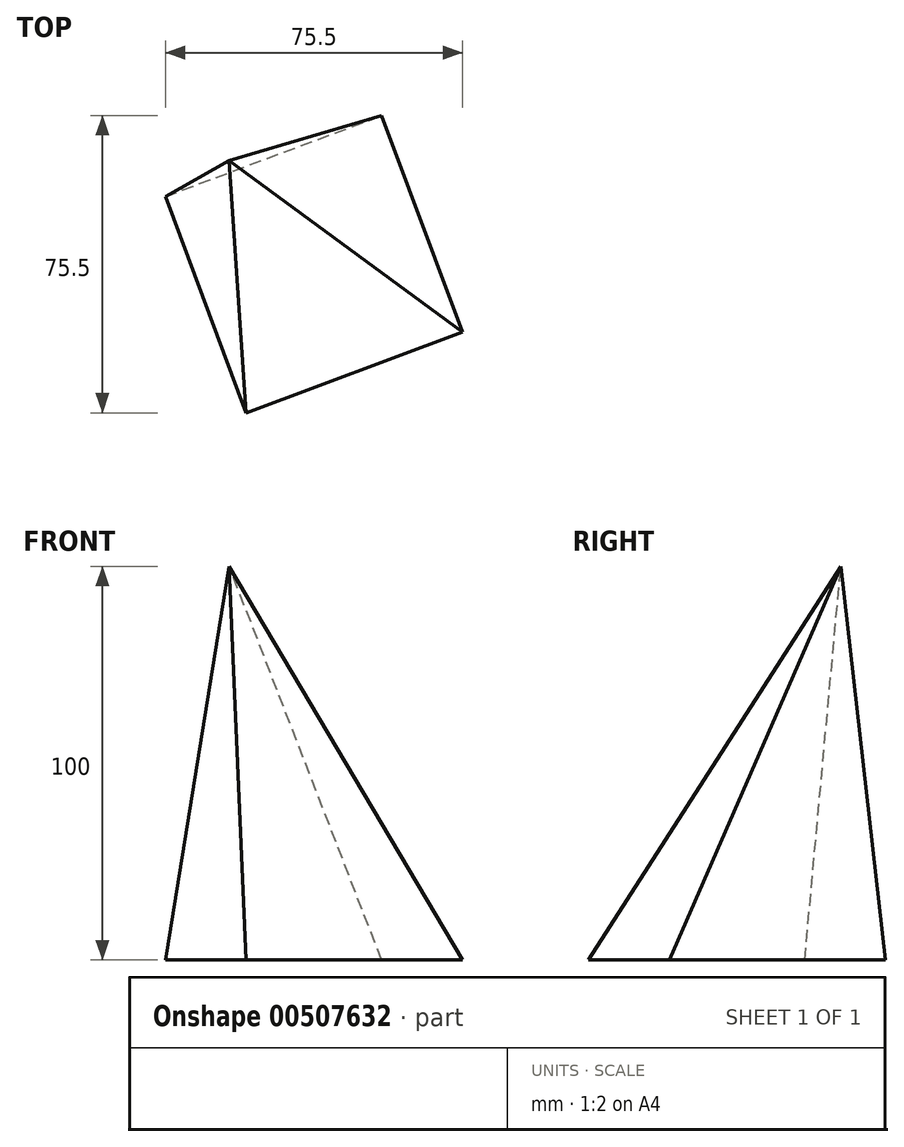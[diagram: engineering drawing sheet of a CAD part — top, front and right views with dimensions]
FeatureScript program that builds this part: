
annotation { "Feature Type Name" : "Feature", "Feature Type Description" : "" }
export const myFeature = defineFeature(function(context is Context, id is Id, definition is map)
    precondition{}
    {
        {
            var Q0;
            Q0=qCreatedBy(makeId("Top.planeOp"),FACE);
            var sketch = newSketch(context, id + "F0", { "sketchPlane" : qUnion([Q0])});
            skCircle(sketch, "E0.cCircle", {"center": v(0, 0) * mm, "radius": 41.48 * mm, "construction": true});
            skLineSegment(sketch, "E0.0", {"start": v(-17.2, -37.75) * mm, "end": v(-37.75, 17.2) * mm});
            skLineSegment(sketch, "E0.1", {"start": v(-37.75, 17.2) * mm, "end": v(17.2, 37.75) * mm});
            skLineSegment(sketch, "E0.2", {"start": v(17.2, 37.75) * mm, "end": v(37.75, -17.2) * mm});
            skLineSegment(sketch, "E0.3", {"start": v(37.75, -17.2) * mm, "end": v(-17.2, -37.75) * mm});
            skSolve(sketch);
        }
        {
            var Q0;
            Q0=qCreatedBy(makeId("Top.planeOp"),FACE);
            cPlane(context, id + "F1", {"entities" : qUnion([Q0]), "cplaneType" : CPlaneType.OFFSET, "offset" : 100 * mm, "width" : 152.4 * mm, "height" : 152.4 * mm});
        }
        {
            var Q0;
            Q0=qCreatedBy(id+"F1.planeOp",FACE);
            var sketch = newSketch(context, id + "F2", { "sketchPlane" : qUnion([Q0])});
            skPoint(sketch, "E1", {"position": v(-21.53, 26.36) * mm});
            skSolve(sketch);
        }
        {
            var Q0;
            Q0=makeQuery(id+"F0.imprint","IMPRINT",FACE,{"disambiguationData":[TD([[makeQuery(id+"F0.imprint","IMPRINT",EDGE,{"derivedFrom":sQuery(id+"F0.wireOp",EDGE,"E0.0")}),-1.0]])]});
            var Q1;
            Q1=sQuery(id+"F2.wireOp",VERTEX,"E1");
            loft(context, id + "F3", {"sheetProfilesArray" : [{ "sheetProfileEntities" : qUnion([Q0]) }, { "sheetProfileEntities" : qUnion([Q1]) }]});
        }
    });
